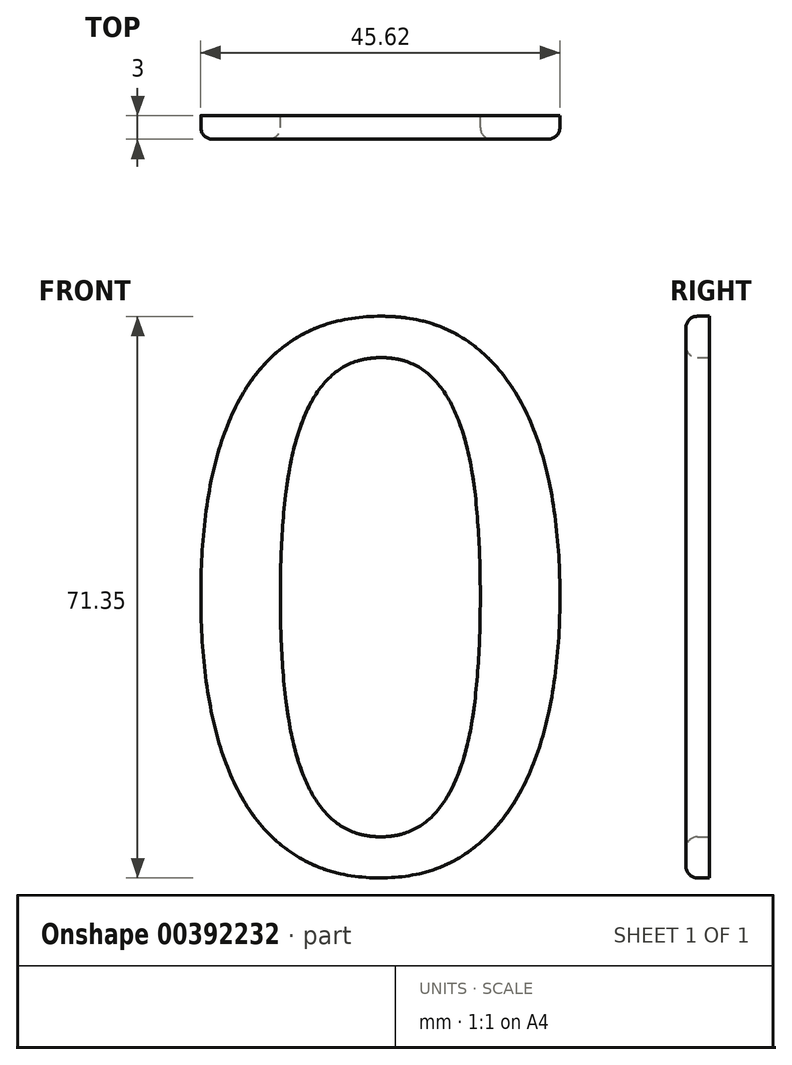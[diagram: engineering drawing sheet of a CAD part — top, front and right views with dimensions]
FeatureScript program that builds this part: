
annotation { "Feature Type Name" : "Feature", "Feature Type Description" : "" }
export const myFeature = defineFeature(function(context is Context, id is Id, definition is map)
    precondition{}
    {
        {
            var Q0;
            Q0=qCreatedBy(makeId("Front.planeOp"),FACE);
            var sketch = newSketch(context, id + "F0", { "sketchPlane" : qUnion([Q0])});
            skText(sketch, "E0", { "text": "0", "fontName": "NotoSerif-Regular.ttf"});
            const initialGuessF0  = {"E0": [0, 0, 1, 0, 0.07]};
            skSetInitialGuess(sketch, initialGuessF0);
            skSolve(sketch);
        }
        {
            var Q0;
            Q0 = qSketchRegion(id + "F0", true);
            extrude(context, id + "F1", {"entities" : qUnion([Q0]), "depth" : 3 * mm});
        }
        {
            var Q0;
            Q0=makeQuery(id+"F1.opExtrude","CAP_FACE",FACE,{"disambiguationData":[OSD([sQuery(id+"F0.wireOp",EDGE,"E0.sketch_text.stroke-0"),sQuery(id+"F0.wireOp",EDGE,"E0.sketch_text.stroke-1"),sQuery(id+"F0.wireOp",EDGE,"E0.sketch_text.stroke-2"),sQuery(id+"F0.wireOp",EDGE,"E0.sketch_text.stroke-3"),sQuery(id+"F0.wireOp",EDGE,"E0.sketch_text.stroke-4"),sQuery(id+"F0.wireOp",EDGE,"E0.sketch_text.stroke-5"),sQuery(id+"F0.wireOp",EDGE,"E0.sketch_text.stroke-6"),sQuery(id+"F0.wireOp",EDGE,"E0.sketch_text.stroke-7"),sQuery(id+"F0.wireOp",EDGE,"E0.sketch_text.stroke-8"),sQuery(id+"F0.wireOp",EDGE,"E0.sketch_text.stroke-9"),sQuery(id+"F0.wireOp",EDGE,"E0.sketch_text.stroke-10"),sQuery(id+"F0.wireOp",EDGE,"E0.sketch_text.stroke-11"),sQuery(id+"F0.wireOp",EDGE,"E0.sketch_text.stroke-12"),sQuery(id+"F0.wireOp",EDGE,"E0.sketch_text.stroke-13"),sQuery(id+"F0.wireOp",EDGE,"E0.sketch_text.stroke-14"),sQuery(id+"F0.wireOp",EDGE,"E0.sketch_text.stroke-15"),sQuery(id+"F0.wireOp",EDGE,"E0.sketch_text.stroke-16"),sQuery(id+"F0.wireOp",EDGE,"E0.sketch_text.stroke-17"),sQuery(id+"F0.wireOp",EDGE,"E0.sketch_text.stroke-18"),sQuery(id+"F0.wireOp",EDGE,"E0.sketch_text.stroke-19"),sQuery(id+"F0.wireOp",EDGE,"E0.sketch_text.stroke-20"),sQuery(id+"F0.wireOp",EDGE,"E0.sketch_text.stroke-21"),sQuery(id+"F0.wireOp",EDGE,"E0.sketch_text.stroke-22"),sQuery(id+"F0.wireOp",EDGE,"E0.sketch_text.stroke-23"),sQuery(id+"F0.wireOp",EDGE,"E0.sketch_text.stroke-24"),sQuery(id+"F0.wireOp",EDGE,"E0.sketch_text.stroke-25"),sQuery(id+"F0.wireOp",EDGE,"E0.sketch_text.stroke-26"),sQuery(id+"F0.wireOp",EDGE,"E0.sketch_text.stroke-27"),sQuery(id+"F0.wireOp",EDGE,"E0.sketch_text.stroke-28"),sQuery(id+"F0.wireOp",EDGE,"E0.sketch_text.stroke-29"),sQuery(id+"F0.wireOp",EDGE,"E0.sketch_text.stroke-30"),sQuery(id+"F0.wireOp",EDGE,"E0.sketch_text.stroke-31")])],"isStart":false});
            fillet(context, id + "F2", {"entities" : qUnion([Q0]), "radius" : 1.5 * mm, "tangentPropagation" : true, "allowEdgeOverflow" : false});
        }
    });
